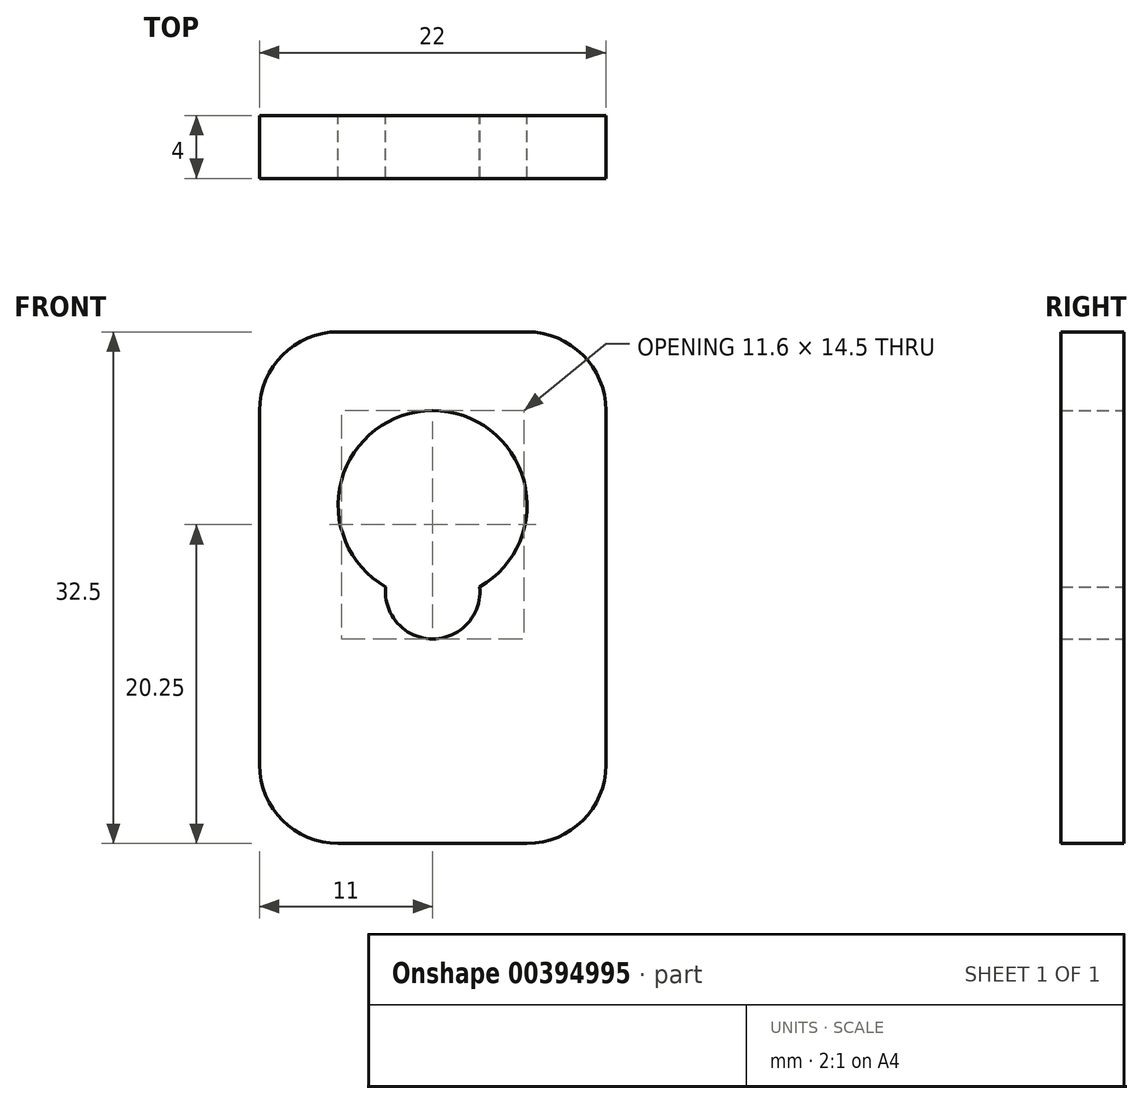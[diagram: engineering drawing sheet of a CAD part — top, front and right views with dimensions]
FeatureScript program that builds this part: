
annotation { "Feature Type Name" : "Feature", "Feature Type Description" : "" }
export const myFeature = defineFeature(function(context is Context, id is Id, definition is map)
    precondition{}
    {
        {
            var Q0;
            Q0=qCreatedBy(makeId("Front.planeOp"),FACE);
            var sketch = newSketch(context, id + "F0", { "sketchPlane" : qUnion([Q0])});
            skArc(sketch, "E0", {"start": v(2.99, -5.2) * mm, "mid": v(0, 6) * mm, "end": v(-2.99, -5.2) * mm});
            skArc(sketch, "E1", {"start": v(-2.99, -5.2) * mm, "mid": v(0, -8.5) * mm, "end": v(2.99, -5.2) * mm});
            skSolve(sketch);
        }
        {
            var Q0;
            Q0=qCreatedBy(makeId("Front.planeOp"),FACE);
            var sketch = newSketch(context, id + "F1", { "sketchPlane" : qUnion([Q0])});
            skLineSegment(sketch, "E2.bottom", {"start": v(-6, 6) * mm, "end": v(6, 6) * mm, "construction": true});
            skLineSegment(sketch, "E2.top", {"start": v(-6, -16.5) * mm, "end": v(6, -16.5) * mm, "construction": true});
            skLineSegment(sketch, "E2.left", {"start": v(-6, 6) * mm, "end": v(-6, -16.5) * mm, "construction": true});
            skLineSegment(sketch, "E2.right", {"start": v(6, 6) * mm, "end": v(6, -16.5) * mm, "construction": true});
            skLineSegment(sketch, "E3.0", {"start": v(11, 11) * mm, "end": v(11, -21.5) * mm});
            skLineSegment(sketch, "E3.1", {"start": v(-11, 11) * mm, "end": v(11, 11) * mm});
            skLineSegment(sketch, "E3.2", {"start": v(-11, 11) * mm, "end": v(-11, -21.5) * mm});
            skLineSegment(sketch, "E3.3", {"start": v(-11, -21.5) * mm, "end": v(11, -21.5) * mm});
            skSolve(sketch);
        }
        {
            var Q0;
            Q0 = qSketchRegion(id + "F1", true);
            extrude(context, id + "F2", {"entities" : qUnion([Q0]), "depth" : 4 * mm});
        }
        {
            var Q0;
            Q0 = qSketchRegion(id + "F0", true);
            extrude(context, id + "F3", {"entities" : qUnion([Q0]), "operationType" : NewBodyOperationType.REMOVE, "endBound" : BoundingType.THROUGH_ALL, "depth" : 25 * mm});
        }
        {
            var Q0;
            Q0=makeQuery(id+"F2.opExtrude","SWEPT_EDGE",EDGE,{"disambiguationData":[OSD([sQuery(id+"F1.wireOp",EDGE,"E3.0"),sQuery(id+"F1.wireOp",EDGE,"E3.1")])]});
            var Q1;
            Q1=makeQuery(id+"F2.opExtrude","SWEPT_EDGE",EDGE,{"disambiguationData":[OSD([sQuery(id+"F1.wireOp",EDGE,"E3.1"),sQuery(id+"F1.wireOp",EDGE,"E3.2")])]});
            var Q2;
            Q2=makeQuery(id+"F2.opExtrude","SWEPT_EDGE",EDGE,{"disambiguationData":[OSD([sQuery(id+"F1.wireOp",EDGE,"E3.2"),sQuery(id+"F1.wireOp",EDGE,"E3.3")])]});
            var Q3;
            Q3=makeQuery(id+"F2.opExtrude","SWEPT_EDGE",EDGE,{"disambiguationData":[OSD([sQuery(id+"F1.wireOp",EDGE,"E3.0"),sQuery(id+"F1.wireOp",EDGE,"E3.3")])]});
            fillet(context, id + "F4", {"entities" : qUnion([Q0, Q1, Q2, Q3]), "radius" : 5 * mm, "tangentPropagation" : true, "allowEdgeOverflow" : false});
        }
    });
